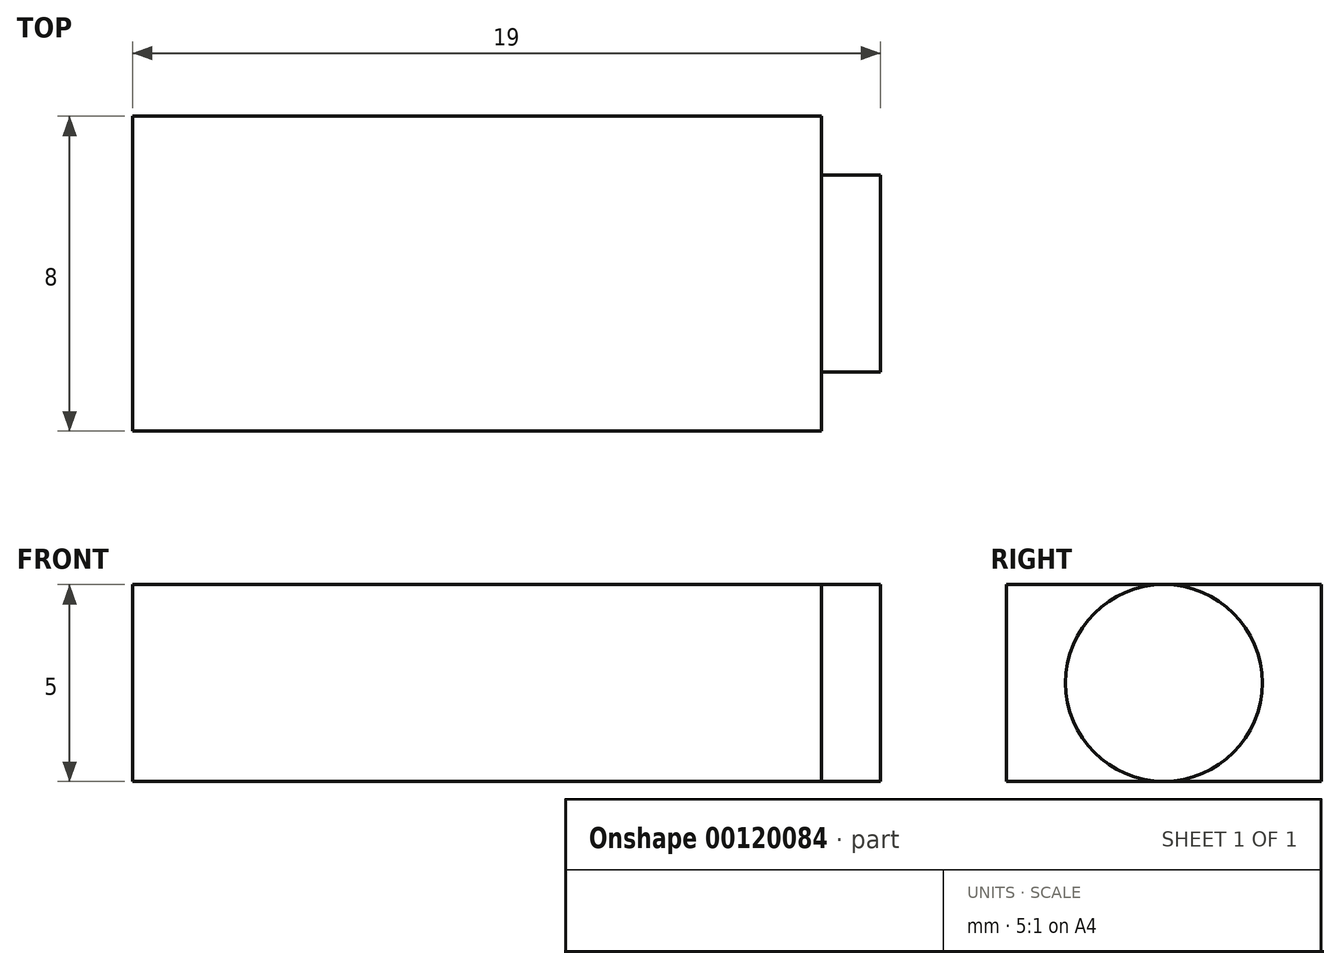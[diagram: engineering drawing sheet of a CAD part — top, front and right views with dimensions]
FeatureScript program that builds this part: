
annotation { "Feature Type Name" : "Feature", "Feature Type Description" : "" }
export const myFeature = defineFeature(function(context is Context, id is Id, definition is map)
    precondition{}
    {
        {
            var Q0;
            Q0=qCreatedBy(makeId("Front.planeOp"),FACE);
            var sketch = newSketch(context, id + "F0", { "sketchPlane" : qUnion([Q0])});
            skLineSegment(sketch, "E0.bottom", {"start": v(-19, 5) * mm, "end": v(-1.5, 5) * mm});
            skLineSegment(sketch, "E0.top", {"start": v(-19, 0) * mm, "end": v(-1.5, 0) * mm});
            skLineSegment(sketch, "E0.left", {"start": v(-19, 5) * mm, "end": v(-19, 0) * mm});
            skLineSegment(sketch, "E0.right", {"start": v(-1.5, 5) * mm, "end": v(-1.5, 0) * mm});
            skSolve(sketch);
        }
        {
            var Q0;
            Q0 = qSketchRegion(id + "F0", true);
            extrude(context, id + "F1", {"entities" : qUnion([Q0]), "endBound" : BoundingType.SYMMETRIC, "depth" : 8 * mm});
        }
        {
            var Q0;
            Q0=makeQuery(id+"F1.opExtrude","SWEPT_FACE",FACE,{"disambiguationData":[OSD([sQuery(id+"F0.wireOp",EDGE,"E0.right")])]});
            var sketch = newSketch(context, id + "F2", { "sketchPlane" : qUnion([Q0])});
            skCircle(sketch, "E1", {"center": v(0, 2.5) * mm, "radius": 2.5 * mm});
            skPoint(sketch, "E1.centerSnap0", {"position": v(-4, 2.5) * mm});
            skSolve(sketch);
        }
        {
            var Q0;
            {var subQ0=sQuery(id+"F2.wireOp",EDGE,"E1");var subQ1=sQuery(id+"F0.wireOp",EDGE,"E0.right");var subQ2=makeQuery(id+"F2.imprint","INTERSECT",VERTEX,{"derivedFrom":[makeQuery(id+"F1.opExtrude","SWEPT_EDGE",EDGE,{"disambiguationData":[OSD([sQuery(id+"F0.wireOp",EDGE,"E0.bottom"),subQ1])]}),subQ0]});Q0=makeQuery(id+"F2.imprint","IMPRINT",FACE,{"disambiguationData":[TD([[makeQuery(id+"F2.imprint","IMPRINT",EDGE,{"disambiguationData":[TD([[subQ2,-1.0]])],"derivedFrom":subQ0}),1.0]])]});}
            extrude(context, id + "F3", {"entities" : qUnion([Q0]), "operationType" : NewBodyOperationType.ADD, "depth" : 1.5 * mm});
        }
    });
